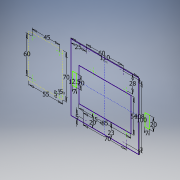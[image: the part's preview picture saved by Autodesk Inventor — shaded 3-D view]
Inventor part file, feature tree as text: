
AUTODESK INVENTOR PART (.ipt)
format: ipt  version: 2019 (Build 230136000, 136)  size: 120,320 bytes
history: native  units: mm
features: sketch x1
ambient origin geometry x8: Origin, YZ Plane, XZ Plane, XY Plane, X Axis, Y Axis, Z Axis, Center Point
feature tree (1):
  sketch  "Sketch1"  dims[d0=60.0mm d1=100.0mm d2=70.0mm d3=110.0mm d4=108.0mm d6=35.0mm d7=5.0mm d8=85.0mm d9=54.0mm d10=25.0mm d11=45.0mm d12=60.0mm d13=12.5mm d14=23.0mm d15=55.0mm d16=70.0mm d17=5.0mm d18=5.0mm d23=28.0mm d24=20.0mm d29=7.0mm d30=20.0mm d31=7.0mm d32=20.0mm]
